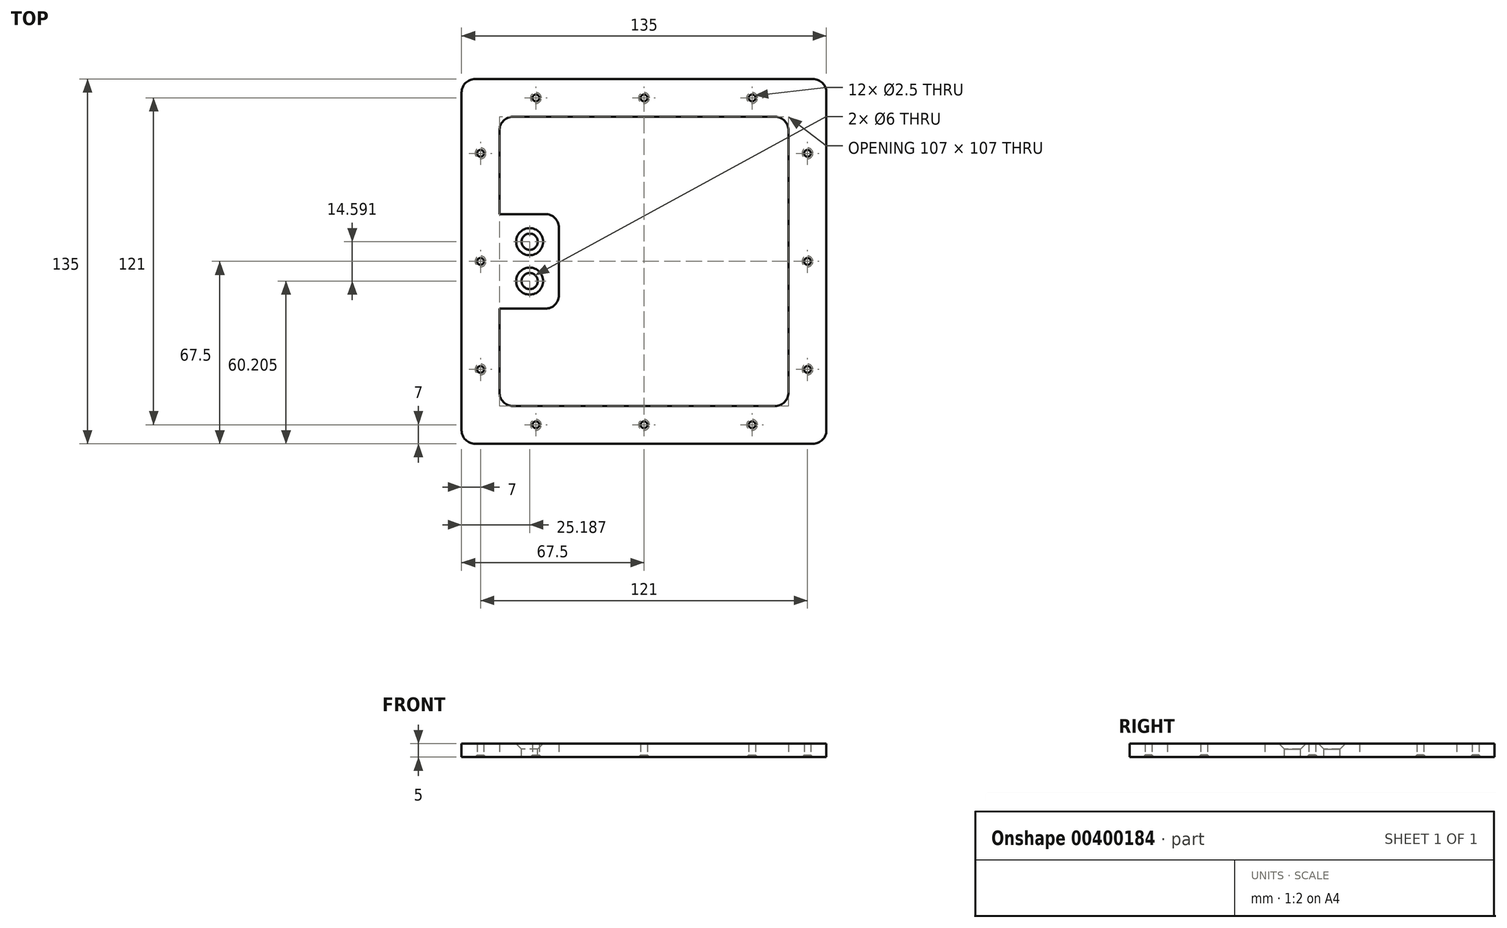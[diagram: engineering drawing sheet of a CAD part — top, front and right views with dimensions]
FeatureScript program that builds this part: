
annotation { "Feature Type Name" : "Feature", "Feature Type Description" : "" }
export const myFeature = defineFeature(function(context is Context, id is Id, definition is map)
    precondition{}
    {
        {
            var Q0;
            Q0=qCreatedBy(makeId("Top.planeOp"),FACE);
            var sketch = newSketch(context, id + "F0", { "sketchPlane" : qUnion([Q0])});
            skLineSegment(sketch, "E0.bottom", {"start": v(67.5, -67.5) * mm, "end": v(-67.5, -67.5) * mm});
            skLineSegment(sketch, "E0.top", {"start": v(67.5, 67.5) * mm, "end": v(-67.5, 67.5) * mm});
            skLineSegment(sketch, "E0.left", {"start": v(67.5, -67.5) * mm, "end": v(67.5, 67.5) * mm});
            skLineSegment(sketch, "E0.right", {"start": v(-67.5, -67.5) * mm, "end": v(-67.5, 67.5) * mm});
            skPoint(sketch, "E0.middle", {"position": v(0, 0) * mm});
            skLineSegment(sketch, "E1.bottom", {"start": v(-53.5, 53.5) * mm, "end": v(53.5, 53.5) * mm});
            skLineSegment(sketch, "E1.top", {"start": v(-53.5, -53.5) * mm, "end": v(53.5, -53.5) * mm});
            skLineSegment(sketch, "E1.left", {"start": v(-53.5, 53.5) * mm, "end": v(-53.5, -53.5) * mm});
            skLineSegment(sketch, "E1.right", {"start": v(53.5, 53.5) * mm, "end": v(53.5, -53.5) * mm});
            skLineSegment(sketch, "E2", {"start": v(-53.5, 17.5) * mm, "end": v(-31.5, 17.5) * mm});
            skLineSegment(sketch, "E3", {"start": v(-31.5, 17.5) * mm, "end": v(-31.5, 0) * mm});
            skLineSegment(sketch, "E4", {"start": v(-31.5, 0) * mm, "end": v(-31.5, -17.5) * mm});
            skLineSegment(sketch, "E5", {"start": v(-31.5, -17.5) * mm, "end": v(-53.5, -17.5) * mm});
            skLineSegment(sketch, "E6", {"start": v(53.5, 0) * mm, "end": v(53.5, 17.5) * mm});
            skLineSegment(sketch, "E7", {"start": v(53.5, 17.5) * mm, "end": v(33.5, 17.5) * mm});
            skLineSegment(sketch, "E8", {"start": v(33.5, 17.5) * mm, "end": v(33.5, 0) * mm});
            skLineSegment(sketch, "E9", {"start": v(33.5, 0) * mm, "end": v(33.5, -17.5) * mm});
            skLineSegment(sketch, "E10", {"start": v(33.5, -17.5) * mm, "end": v(53.5, -17.5) * mm});
            skLineSegment(sketch, "E11", {"start": v(53.5, -17.5) * mm, "end": v(53.5, 0) * mm});
            skLineSegment(sketch, "E12", {"start": v(-67.5, 0) * mm, "end": v(-67.5, 15) * mm});
            skLineSegment(sketch, "E13", {"start": v(-67.5, 15) * mm, "end": v(-85, 15) * mm});
            skLineSegment(sketch, "E14", {"start": v(-85, 15) * mm, "end": v(-85, 0) * mm});
            skLineSegment(sketch, "E15", {"start": v(-85, 0) * mm, "end": v(-85, -15) * mm});
            skLineSegment(sketch, "E16", {"start": v(-85, -15) * mm, "end": v(-67.5, -15) * mm});
            skLineSegment(sketch, "E17", {"start": v(67.5, 0) * mm, "end": v(67.5, 15) * mm});
            skLineSegment(sketch, "E18", {"start": v(67.5, 15) * mm, "end": v(85, 15) * mm});
            skLineSegment(sketch, "E19", {"start": v(85, 15) * mm, "end": v(85, 0) * mm});
            skLineSegment(sketch, "E20", {"start": v(85, 0) * mm, "end": v(85, -15) * mm});
            skLineSegment(sketch, "E21", {"start": v(85, -15) * mm, "end": v(67.5, -15) * mm});
            skPoint(sketch, "E22", {"position": v(-60.5, 0) * mm});
            skPoint(sketch, "E23", {"position": v(-60.5, 40) * mm});
            skPoint(sketch, "E24", {"position": v(-60.5, -40) * mm});
            skPoint(sketch, "E25", {"position": v(0, -60.5) * mm});
            skPoint(sketch, "E26", {"position": v(40, -60.5) * mm});
            skPoint(sketch, "E27", {"position": v(-40, -60.5) * mm});
            skPoint(sketch, "E28", {"position": v(60.5, 0) * mm});
            skPoint(sketch, "E29", {"position": v(60.5, -40) * mm});
            skPoint(sketch, "E30", {"position": v(60.5, 40) * mm});
            skPoint(sketch, "E31", {"position": v(0, 60.5) * mm});
            skPoint(sketch, "E32", {"position": v(40, 60.5) * mm});
            skPoint(sketch, "E33", {"position": v(-40, 60.5) * mm});
            skPoint(sketch, "E34", {"position": v(80, 10) * mm});
            skPoint(sketch, "E35", {"position": v(80, -10) * mm});
            skPoint(sketch, "E36", {"position": v(-80, 10) * mm});
            skPoint(sketch, "E37", {"position": v(-80, -10) * mm});
            skSolve(sketch);
        }
        {
            var Q0;
            {var subQ0=sQuery(id+"F0.wireOp",EDGE,"E12");Q0=makeQuery(id+"F0.imprint","IMPRINT",FACE,{"disambiguationData":[TD([[makeQuery(id+"F0.imprint","IMPRINT",EDGE,{"derivedFrom":subQ0}),1.0]])]});}
            var Q1;
            {var subQ0=sQuery(id+"F0.wireOp",EDGE,"E2");Q1=makeQuery(id+"F0.imprint","IMPRINT",FACE,{"disambiguationData":[TD([[makeQuery(id+"F0.imprint","IMPRINT",EDGE,{"derivedFrom":subQ0}),-1.0]])]});}
            var Q2;
            {var subQ7=sQuery(id+"F0.wireOp",EDGE,"E0.bottom");Q2=makeQuery(id+"F0.imprint","IMPRINT",FACE,{"disambiguationData":[TD([[makeQuery(id+"F0.imprint","IMPRINT",EDGE,{"derivedFrom":subQ7}),-1.0]])]});}
            var Q3;
            Q3=makeQuery(id+"F0.imprint","IMPRINT",FACE,{"disambiguationData":[TD([[makeQuery(id+"F0.imprint","IMPRINT",EDGE,{"derivedFrom":sQuery(id+"F0.wireOp",EDGE,"E6")}),1.0]])]});
            var Q4;
            {var subQ0=sQuery(id+"F0.wireOp",EDGE,"E17");Q4=makeQuery(id+"F0.imprint","IMPRINT",FACE,{"disambiguationData":[TD([[makeQuery(id+"F0.imprint","IMPRINT",EDGE,{"derivedFrom":subQ0}),-1.0]])]});}
            extrude(context, id + "F1", {"entities" : qUnion([Q0, Q1, Q2, Q3, Q4]), "depth" : 5 * mm});
        }
        {
            var Q0;
            Q0=sQuery(id+"F0.wireOp",VERTEX,"E22");
            var Q1;
            Q1=sQuery(id+"F0.wireOp",VERTEX,"E24");
            var Q2;
            Q2=sQuery(id+"F0.wireOp",VERTEX,"E23");
            var Q3;
            Q3=sQuery(id+"F0.wireOp",VERTEX,"E33");
            var Q4;
            Q4=sQuery(id+"F0.wireOp",VERTEX,"E31");
            var Q5;
            Q5=sQuery(id+"F0.wireOp",VERTEX,"E32");
            var Q6;
            Q6=sQuery(id+"F0.wireOp",VERTEX,"E30");
            var Q7;
            Q7=sQuery(id+"F0.wireOp",VERTEX,"E28");
            var Q8;
            Q8=sQuery(id+"F0.wireOp",VERTEX,"E29");
            var Q9;
            Q9=sQuery(id+"F0.wireOp",VERTEX,"E26");
            var Q10;
            Q10=sQuery(id+"F0.wireOp",VERTEX,"E25");
            var Q11;
            Q11=sQuery(id+"F0.wireOp",VERTEX,"E27");
            var Q12;
            Q12=sQuery(id+"F0.wireOp",VERTEX,"E37");
            var Q13;
            Q13=sQuery(id+"F0.wireOp",VERTEX,"E36");
            var Q14;
            Q14=sQuery(id+"F0.wireOp",VERTEX,"E35");
            var Q15;
            Q15=sQuery(id+"F0.wireOp",VERTEX,"E34");
            var Q16;
            Q16=makeQuery(id+"F1.opExtrude","SWEPT_BODY",BODY,{"disambiguationData":[OSD([sQuery(id+"F0.wireOp",EDGE,"E0.bottom"),sQuery(id+"F0.wireOp",EDGE,"E0.top"),sQuery(id+"F0.wireOp",EDGE,"E0.left"),sQuery(id+"F0.wireOp",EDGE,"E0.right"),sQuery(id+"F0.wireOp",EDGE,"E1.bottom"),sQuery(id+"F0.wireOp",EDGE,"E1.top"),sQuery(id+"F0.wireOp",EDGE,"E1.left"),sQuery(id+"F0.wireOp",EDGE,"E1.right"),sQuery(id+"F0.wireOp",EDGE,"E2"),sQuery(id+"F0.wireOp",EDGE,"E3"),sQuery(id+"F0.wireOp",EDGE,"E4"),sQuery(id+"F0.wireOp",EDGE,"E5"),sQuery(id+"F0.wireOp",EDGE,"E7"),sQuery(id+"F0.wireOp",EDGE,"E8"),sQuery(id+"F0.wireOp",EDGE,"E9"),sQuery(id+"F0.wireOp",EDGE,"E10"),sQuery(id+"F0.wireOp",EDGE,"E13"),sQuery(id+"F0.wireOp",EDGE,"E14"),sQuery(id+"F0.wireOp",EDGE,"E15"),sQuery(id+"F0.wireOp",EDGE,"E16"),sQuery(id+"F0.wireOp",EDGE,"E18"),sQuery(id+"F0.wireOp",EDGE,"E19"),sQuery(id+"F0.wireOp",EDGE,"E20"),sQuery(id+"F0.wireOp",EDGE,"E21")])]});
            hole(context, id + "F2", {"style" : HoleStyle.C_SINK, "endStyle" : HoleEndStyle.THROUGH, "oppositeDirection" : true, "holeDiameter" : 2.5 * mm, "cSinkDiameter" : 4 * mm, "cSinkAngle" : 90 * degree, "isTappedThrough" : true, "tappedDepth" : 12 * mm, "tapClearance" : 3, "locations" : qUnion([Q0, Q1, Q2, Q3, Q4, Q5, Q6, Q7, Q8, Q9, Q10, Q11, Q12, Q13, Q14, Q15]), "scope" : qUnion([Q16])});
        }
        {
            var Q0;
            Q0=makeQuery(id+"F1.opExtrude","SWEPT_EDGE",EDGE,{"disambiguationData":[OSD([sQuery(id+"F0.wireOp",EDGE,"E2"),sQuery(id+"F0.wireOp",EDGE,"E3")])]});
            var Q1;
            Q1=makeQuery(id+"F1.opExtrude","SWEPT_EDGE",EDGE,{"disambiguationData":[OSD([sQuery(id+"F0.wireOp",EDGE,"E9"),sQuery(id+"F0.wireOp",EDGE,"E10")])]});
            var Q2;
            Q2=makeQuery(id+"F1.opExtrude","SWEPT_EDGE",EDGE,{"disambiguationData":[OSD([sQuery(id+"F0.wireOp",EDGE,"E7"),sQuery(id+"F0.wireOp",EDGE,"E8")])]});
            var Q3;
            Q3=makeQuery(id+"F1.opExtrude","SWEPT_EDGE",EDGE,{"disambiguationData":[OSD([sQuery(id+"F0.wireOp",EDGE,"E0.top"),sQuery(id+"F0.wireOp",EDGE,"E0.right")])]});
            var Q4;
            Q4=makeQuery(id+"F1.opExtrude","SWEPT_EDGE",EDGE,{"disambiguationData":[OSD([sQuery(id+"F0.wireOp",EDGE,"E0.top"),sQuery(id+"F0.wireOp",EDGE,"E0.left")])]});
            var Q5;
            Q5=makeQuery(id+"F1.opExtrude","SWEPT_EDGE",EDGE,{"disambiguationData":[OSD([sQuery(id+"F0.wireOp",EDGE,"E0.bottom"),sQuery(id+"F0.wireOp",EDGE,"E0.left")])]});
            var Q6;
            Q6=makeQuery(id+"F1.opExtrude","SWEPT_EDGE",EDGE,{"disambiguationData":[OSD([sQuery(id+"F0.wireOp",EDGE,"E4"),sQuery(id+"F0.wireOp",EDGE,"E5")])]});
            var Q7;
            Q7=makeQuery(id+"F1.opExtrude","SWEPT_EDGE",EDGE,{"disambiguationData":[OSD([sQuery(id+"F0.wireOp",EDGE,"E0.bottom"),sQuery(id+"F0.wireOp",EDGE,"E0.right")])]});
            fillet(context, id + "F3", {"entities" : qUnion([Q0, Q1, Q2, Q3, Q4, Q5, Q6, Q7]), "radius" : 5 * mm, "allowEdgeOverflow" : false});
        }
        {
            var Q0;
            Q0=makeQuery(id+"F1.opExtrude","SWEPT_EDGE",EDGE,{"disambiguationData":[OSD([sQuery(id+"F0.wireOp",EDGE,"E1.top"),sQuery(id+"F0.wireOp",EDGE,"E1.left")])]});
            var Q1;
            Q1=makeQuery(id+"F1.opExtrude","SWEPT_EDGE",EDGE,{"disambiguationData":[OSD([sQuery(id+"F0.wireOp",EDGE,"E1.bottom"),sQuery(id+"F0.wireOp",EDGE,"E1.left")])]});
            var Q2;
            Q2=makeQuery(id+"F1.opExtrude","SWEPT_EDGE",EDGE,{"disambiguationData":[OSD([sQuery(id+"F0.wireOp",EDGE,"E1.top"),sQuery(id+"F0.wireOp",EDGE,"E1.right")])]});
            var Q3;
            Q3=makeQuery(id+"F1.opExtrude","SWEPT_EDGE",EDGE,{"disambiguationData":[OSD([sQuery(id+"F0.wireOp",EDGE,"E1.bottom"),sQuery(id+"F0.wireOp",EDGE,"E1.right")])]});
            fillet(context, id + "F4", {"entities" : qUnion([Q0, Q1, Q2, Q3]), "radius" : 5 * mm, "allowEdgeOverflow" : false});
        }
        {
            var Q0;
            Q0=makeQuery(id+"F1.opExtrude","CAP_FACE",FACE,{"disambiguationData":[OSD([sQuery(id+"F0.wireOp",EDGE,"E0.bottom"),sQuery(id+"F0.wireOp",EDGE,"E0.top"),sQuery(id+"F0.wireOp",EDGE,"E0.left"),sQuery(id+"F0.wireOp",EDGE,"E0.right"),sQuery(id+"F0.wireOp",EDGE,"E1.bottom"),sQuery(id+"F0.wireOp",EDGE,"E1.top"),sQuery(id+"F0.wireOp",EDGE,"E1.left"),sQuery(id+"F0.wireOp",EDGE,"E1.right"),sQuery(id+"F0.wireOp",EDGE,"E2"),sQuery(id+"F0.wireOp",EDGE,"E3"),sQuery(id+"F0.wireOp",EDGE,"E4"),sQuery(id+"F0.wireOp",EDGE,"E5"),sQuery(id+"F0.wireOp",EDGE,"E7"),sQuery(id+"F0.wireOp",EDGE,"E8"),sQuery(id+"F0.wireOp",EDGE,"E9"),sQuery(id+"F0.wireOp",EDGE,"E10"),sQuery(id+"F0.wireOp",EDGE,"E13"),sQuery(id+"F0.wireOp",EDGE,"E14"),sQuery(id+"F0.wireOp",EDGE,"E15"),sQuery(id+"F0.wireOp",EDGE,"E16"),sQuery(id+"F0.wireOp",EDGE,"E18"),sQuery(id+"F0.wireOp",EDGE,"E19"),sQuery(id+"F0.wireOp",EDGE,"E20"),sQuery(id+"F0.wireOp",EDGE,"E21")])],"isStart":false});
            var sketch = newSketch(context, id + "F5", { "sketchPlane" : qUnion([Q0])});
            skPoint(sketch, "E38", {"position": v(42.31, 7.3) * mm});
            skPoint(sketch, "E39", {"position": v(42.31, -7.3) * mm});
            skPoint(sketch, "E40", {"position": v(-42.31, 7.3) * mm});
            skPoint(sketch, "E41", {"position": v(-42.31, -7.3) * mm});
            skLineSegment(sketch, "E42.bottom", {"start": v(-70, 70) * mm, "end": v(70, 70) * mm});
            skLineSegment(sketch, "E42.top", {"start": v(-70, -70) * mm, "end": v(70, -70) * mm});
            skLineSegment(sketch, "E42.left", {"start": v(-70, 70) * mm, "end": v(-70, -70) * mm});
            skLineSegment(sketch, "E42.right", {"start": v(70, 70) * mm, "end": v(70, -70) * mm});
            skPoint(sketch, "E42.middle", {"position": v(0, 0) * mm});
            skSolve(sketch);
        }
        {
            var Q0;
            Q0=sQuery(id+"F5.wireOp",VERTEX,"E40");
            var Q1;
            Q1=sQuery(id+"F5.wireOp",VERTEX,"E41");
            var Q2;
            Q2=sQuery(id+"F5.wireOp",VERTEX,"E38");
            var Q3;
            Q3=sQuery(id+"F5.wireOp",VERTEX,"E39");
            var Q4;
            Q4=makeQuery(id+"F1.opExtrude","SWEPT_BODY",BODY,{"disambiguationData":[OSD([sQuery(id+"F0.wireOp",EDGE,"E0.bottom"),sQuery(id+"F0.wireOp",EDGE,"E0.top"),sQuery(id+"F0.wireOp",EDGE,"E0.left"),sQuery(id+"F0.wireOp",EDGE,"E0.right"),sQuery(id+"F0.wireOp",EDGE,"E1.bottom"),sQuery(id+"F0.wireOp",EDGE,"E1.top"),sQuery(id+"F0.wireOp",EDGE,"E1.left"),sQuery(id+"F0.wireOp",EDGE,"E1.right"),sQuery(id+"F0.wireOp",EDGE,"E2"),sQuery(id+"F0.wireOp",EDGE,"E3"),sQuery(id+"F0.wireOp",EDGE,"E4"),sQuery(id+"F0.wireOp",EDGE,"E5"),sQuery(id+"F0.wireOp",EDGE,"E7"),sQuery(id+"F0.wireOp",EDGE,"E8"),sQuery(id+"F0.wireOp",EDGE,"E9"),sQuery(id+"F0.wireOp",EDGE,"E10"),sQuery(id+"F0.wireOp",EDGE,"E13"),sQuery(id+"F0.wireOp",EDGE,"E14"),sQuery(id+"F0.wireOp",EDGE,"E15"),sQuery(id+"F0.wireOp",EDGE,"E16"),sQuery(id+"F0.wireOp",EDGE,"E18"),sQuery(id+"F0.wireOp",EDGE,"E19"),sQuery(id+"F0.wireOp",EDGE,"E20"),sQuery(id+"F0.wireOp",EDGE,"E21")])]});
            hole(context, id + "F6", {"style" : HoleStyle.C_SINK, "endStyle" : HoleEndStyle.BLIND, "holeDiameter" : 6 * mm, "cSinkDiameter" : 10 * mm, "cSinkAngle" : 90 * degree, "holeDepth" : 12 * mm, "isTappedThrough" : true, "tappedDepth" : 12 * mm, "tapClearance" : 3, "startFromSketch" : true, "locations" : qUnion([Q0, Q1, Q2, Q3]), "scope" : qUnion([Q4])});
        }
    });
